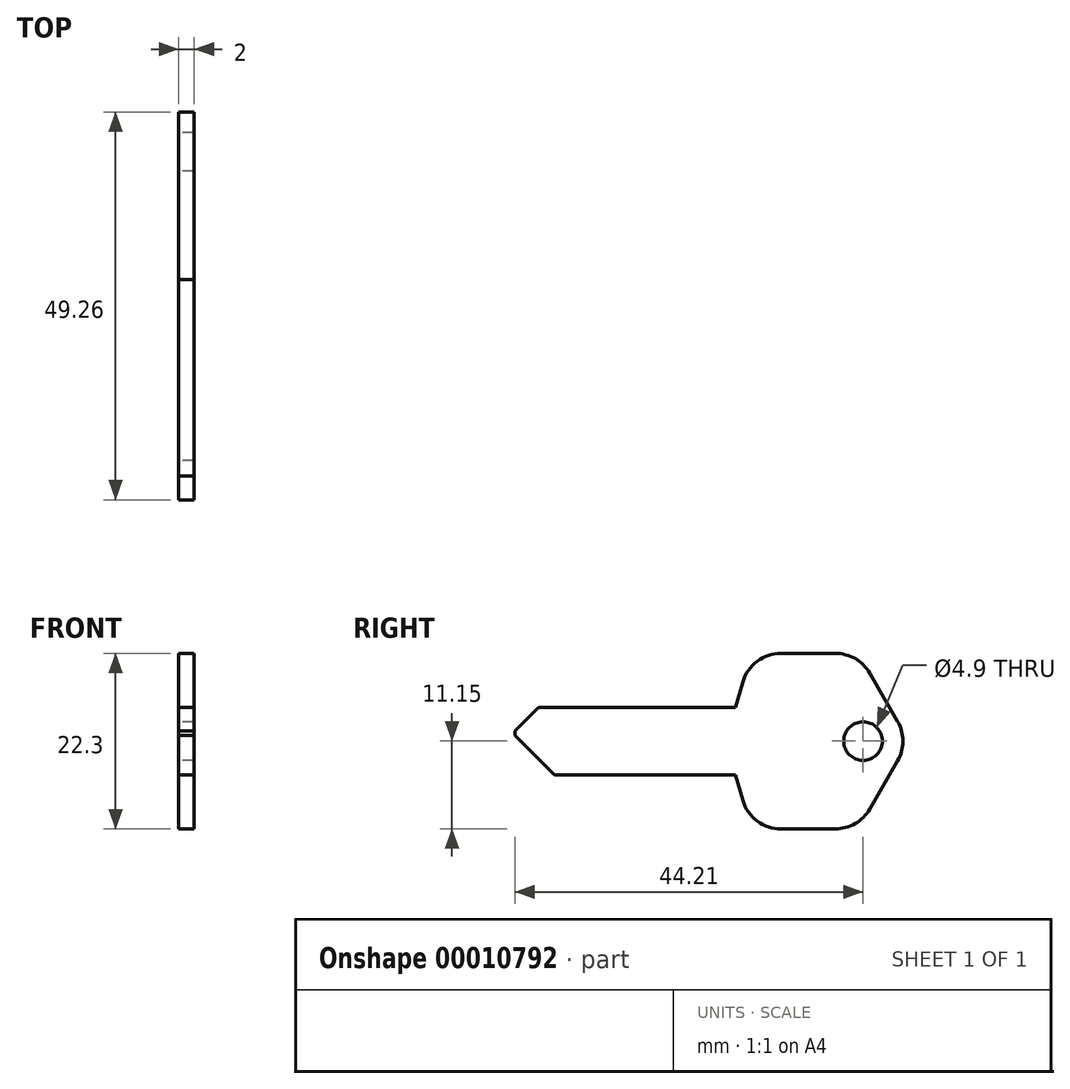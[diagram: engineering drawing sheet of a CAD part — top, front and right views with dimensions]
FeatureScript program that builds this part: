
annotation { "Feature Type Name" : "Feature", "Feature Type Description" : "" }
export const myFeature = defineFeature(function(context is Context, id is Id, definition is map)
    precondition{}
    {
        {
            var Q0;
            Q0=qCreatedBy(makeId("Right.planeOp"),FACE);
            var sketch = newSketch(context, id + "F0", { "sketchPlane" : qUnion([Q0])});
            skCircle(sketch, "E0", {"center": v(0, 0) * mm, "radius": 2.45 * mm});
            skLineSegment(sketch, "E1", {"start": v(0, 0) * mm, "end": v(-32.5, 0) * mm, "construction": true});
            skLineSegment(sketch, "E2", {"start": v(-10.42, 11.15) * mm, "end": v(-3.52, 11.15) * mm});
            skLineSegment(sketch, "E3", {"start": v(0.85, 8.63) * mm, "end": v(4.37, 2.53) * mm});
            skLineSegment(sketch, "E4", {"start": v(4.37, -2.52) * mm, "end": v(0.85, -8.62) * mm});
            skLineSegment(sketch, "E5", {"start": v(-3.52, -11.15) * mm, "end": v(-10.42, -11.15) * mm});
            skLineSegment(sketch, "E6", {"start": v(-15.27, -7.52) * mm, "end": v(-16.2, -4.3) * mm});
            skLineSegment(sketch, "E7", {"start": v(-16.2, -4.3) * mm, "end": v(-44.2, -4.3) * mm});
            skLineSegment(sketch, "E8", {"start": v(-44.2, -4.3) * mm, "end": v(-44.2, 4.3) * mm});
            skLineSegment(sketch, "E9", {"start": v(-44.2, 4.3) * mm, "end": v(-16.2, 4.3) * mm});
            skLineSegment(sketch, "E10", {"start": v(-16.2, 4.3) * mm, "end": v(-15.27, 7.52) * mm});
            skPoint(sketch, "E11.visualSharp", {"position": v(5.83, 0) * mm});
            skArc(sketch, "E11.filletArc", {"start": v(4.37, -2.53) * mm, "mid": v(5.05, 0) * mm, "end": v(4.37, 2.53) * mm});
            skPoint(sketch, "E12.visualSharp", {"position": v(-0.6, 11.15) * mm});
            skArc(sketch, "E12.filletArc", {"start": v(0.85, 8.63) * mm, "mid": v(-1, 10.47) * mm, "end": v(-3.52, 11.15) * mm});
            skPoint(sketch, "E13.visualSharp", {"position": v(-0.6, -11.15) * mm});
            skArc(sketch, "E13.filletArc", {"start": v(-3.52, -11.15) * mm, "mid": v(-1, -10.47) * mm, "end": v(0.85, -8.62) * mm});
            skPoint(sketch, "E14.visualSharp", {"position": v(-14.2, -11.15) * mm});
            skArc(sketch, "E14.filletArc", {"start": v(-15.27, -7.52) * mm, "mid": v(-13.45, -10.14) * mm, "end": v(-10.42, -11.15) * mm});
            skPoint(sketch, "E15.visualSharp", {"position": v(-14.2, 11.15) * mm});
            skArc(sketch, "E15.filletArc", {"start": v(-10.42, 11.15) * mm, "mid": v(-13.45, 10.14) * mm, "end": v(-15.27, 7.52) * mm});
            skSolve(sketch);
        }
        {
            var Q0;
            Q0=makeQuery(id+"F0.imprint","IMPRINT",FACE,{"disambiguationData":[TD([[makeQuery(id+"F0.imprint","IMPRINT",EDGE,{"derivedFrom":sQuery(id+"F0.wireOp",EDGE,"E0")}),-1.0]])]});
            extrude(context, id + "F1", {"entities" : qUnion([Q0]), "depth" : 2 * mm, "symmetric" : true});
        }
        {
            var Q0;
            Q0=makeQuery(id+"F1.opExtrude","SWEPT_EDGE",EDGE,{"disambiguationData":[OSD([sQuery(id+"F0.wireOp",EDGE,"E8"),sQuery(id+"F0.wireOp",EDGE,"E9")])]});
            chamfer(context, id + "F2", {"entities" : qUnion([Q0]), "width" : 3 * mm, "tangentPropagation" : true});
        }
        {
            var Q0;
            Q0=makeQuery(id+"F1.opExtrude","SWEPT_EDGE",EDGE,{"disambiguationData":[OSD([sQuery(id+"F0.wireOp",EDGE,"E7"),sQuery(id+"F0.wireOp",EDGE,"E8")])]});
            chamfer(context, id + "F3", {"entities" : qUnion([Q0]), "width" : 5 * mm, "tangentPropagation" : true});
        }
    });
